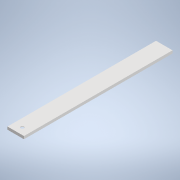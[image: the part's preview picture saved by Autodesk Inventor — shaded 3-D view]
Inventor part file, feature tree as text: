
AUTODESK INVENTOR PART (.ipt)
format: ipt  version: 2022 (Build 260153000, 153)  size: 105,472 bytes
history: native  units: mm
features: sketch x2, other x1, extrude x1, hole x1
ambient origin geometry x8: Origin, YZ Plane, XZ Plane, XY Plane, X Axis, Y Axis, Z Axis, Center Point
bodies: Body1 (feature_tree)
feature tree (5):
  other  "ソリッド1"
  extrude  "押し出し1"  Depth=270.0mm
  hole  "穴1"  [1 undecoded]
  sketch  "スケッチ1"
  sketch  "スケッチ2"
note: 1 required parameter value undecoded (feature->parameter linkage not recoverable at this tier; creation-order binding heuristic only, values carry confidence <= 0.55)
